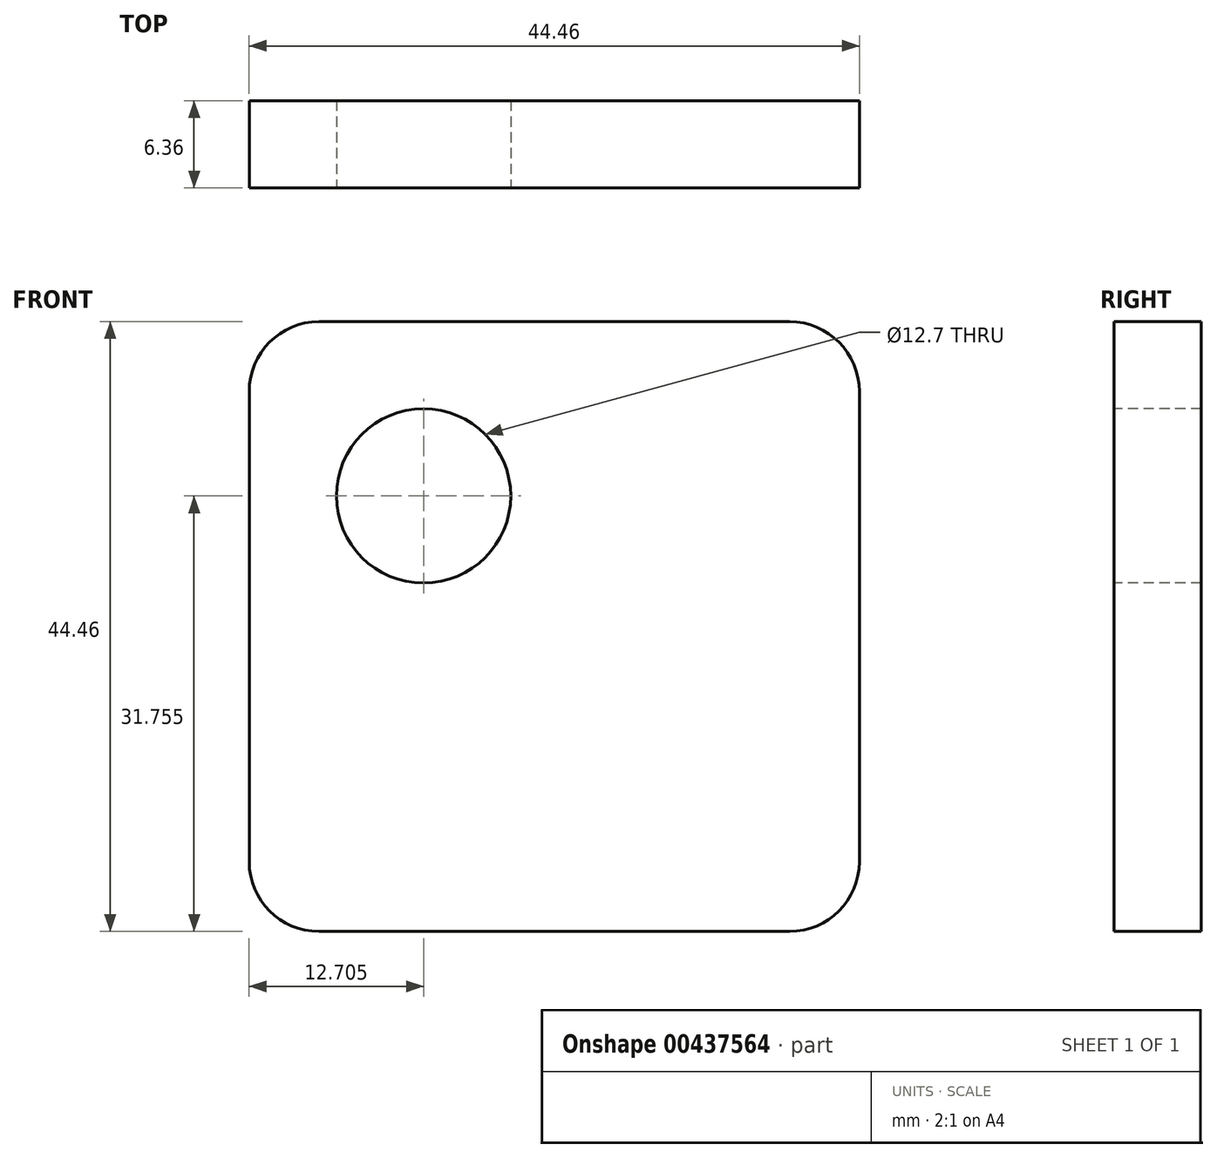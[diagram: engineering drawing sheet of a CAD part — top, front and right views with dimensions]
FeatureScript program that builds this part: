
annotation { "Feature Type Name" : "Feature", "Feature Type Description" : "" }
export const myFeature = defineFeature(function(context is Context, id is Id, definition is map)
    precondition{}
    {
        {
            var Q0;
            Q0=qCreatedBy(makeId("Front.planeOp"),FACE);
            var sketch = newSketch(context, id + "F0", { "sketchPlane" : qUnion([Q0])});
            skLineSegment(sketch, "E0.bottom", {"start": v(22.23, -22.22) * mm, "end": v(-22.23, -22.23) * mm});
            skLineSegment(sketch, "E0.top", {"start": v(22.23, 22.23) * mm, "end": v(-22.23, 22.22) * mm});
            skLineSegment(sketch, "E0.left", {"start": v(22.23, -22.22) * mm, "end": v(22.23, 22.23) * mm});
            skLineSegment(sketch, "E0.right", {"start": v(-22.23, -22.23) * mm, "end": v(-22.23, 22.23) * mm});
            skPoint(sketch, "E0.middle", {"position": v(0, 0) * mm});
            skSolve(sketch);
        }
        {
            var Q0;
            Q0 = qSketchRegion(id + "F0", true);
            extrude(context, id + "F1", {"entities" : qUnion([Q0]), "endBound" : BoundingType.SYMMETRIC, "depth" : 6.35 * mm});
        }
        {
            var Q0;
            Q0=makeQuery(id+"F1.opExtrude","SWEPT_EDGE",EDGE,{"disambiguationData":[OSD([sQuery(id+"F0.wireOp",EDGE,"E0.top"),sQuery(id+"F0.wireOp",EDGE,"E0.right")])]});
            var Q1;
            Q1=makeQuery(id+"F1.opExtrude","SWEPT_EDGE",EDGE,{"disambiguationData":[OSD([sQuery(id+"F0.wireOp",EDGE,"E0.top"),sQuery(id+"F0.wireOp",EDGE,"E0.left")])]});
            var Q2;
            Q2=makeQuery(id+"F1.opExtrude","SWEPT_EDGE",EDGE,{"disambiguationData":[OSD([sQuery(id+"F0.wireOp",EDGE,"E0.bottom"),sQuery(id+"F0.wireOp",EDGE,"E0.left")])]});
            var Q3;
            Q3=makeQuery(id+"F1.opExtrude","SWEPT_EDGE",EDGE,{"disambiguationData":[OSD([sQuery(id+"F0.wireOp",EDGE,"E0.bottom"),sQuery(id+"F0.wireOp",EDGE,"E0.right")])]});
            fillet(context, id + "F2", {"entities" : qUnion([Q0, Q1, Q2, Q3]), "radius" : 5.08 * mm, "tangentPropagation" : true, "allowEdgeOverflow" : false});
        }
        {
            var Q0;
            Q0=makeQuery(id+"F1.opExtrude","CAP_FACE",FACE,{"disambiguationData":[OSD([sQuery(id+"F0.wireOp",EDGE,"E0.bottom"),sQuery(id+"F0.wireOp",EDGE,"E0.top"),sQuery(id+"F0.wireOp",EDGE,"E0.left"),sQuery(id+"F0.wireOp",EDGE,"E0.right")])],"isStart":false});
            var sketch = newSketch(context, id + "F3", { "sketchPlane" : qUnion([Q0])});
            skCircle(sketch, "E1", {"center": v(-9.53, 9.52) * mm, "radius": 6.35 * mm});
            skSolve(sketch);
        }
        {
            var Q0;
            Q0 = qSketchRegion(id + "F3", true);
            extrude(context, id + "F4", {"entities" : qUnion([Q0]), "operationType" : NewBodyOperationType.REMOVE, "endBound" : BoundingType.THROUGH_ALL, "oppositeDirection" : true, "depth" : 25.4 * mm});
        }
    });
